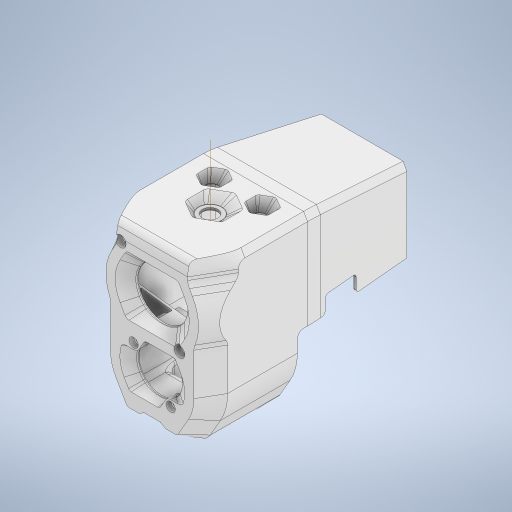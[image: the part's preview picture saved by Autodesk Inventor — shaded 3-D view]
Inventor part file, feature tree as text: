
AUTODESK INVENTOR PART (.ipt)
format: ipt  version: 2024 (Build 280153000, 153)  size: 3,584,000 bytes
history: native  units: mm
features: extrude x39, projected_geometry x35, plane x22, fillet x16, sketch x14, other x8, loft x5, hole x5, sweep x4, mirror x4, shell x4, boolean_combine x3, thicken_offset x3, chamfer x2, surface_op x2, split x1
ambient origin geometry x8: Origin, YZ Plane, XZ Plane, XY Plane, X Axis, Y Axis, Z Axis, Center Point
bodies: Solid1 (feature_tree), Solid4 (feature_tree), Solid5 (feature_tree), Solid2 (feature_tree), Solid3 (feature_tree)
feature tree (167):
  sketch  "Sketch1"  dims[d0=29.0mm d1=24.0mm]
  plane  "Work Plane10"
  extrude  "Extrusion1"  Depth=24.0mm
  plane  "Work Plane1"
  extrude  "Extrusion3"  Depth=7.25mm
  extrude  "Extrusion4"  Depth=33.0mm
  extrude  "Extrusion5"  Depth=30.0mm
  extrude  "Extrusion6"  Depth=20.0mm
  plane  "Work Plane12"
  extrude  "Extrusion16"  Depth=20.0mm
  plane  "Work Plane13"
  plane  "Work Plane14"
  sketch  "3D Sketch3"
  plane  "Work Plane3"
  extrude  "Extrusion17"  Depth=1.22173mm
  extrude  "Extrusion18"  Depth=0.25mm
  plane  "Work Plane15"
  sweep  "Sweep7"
  sketch  "3D Sketch5"
  sweep  "Sweep8"
  sweep  "Sweep9"
  mirror  "Mirror5"
  chamfer  "Chamfer4"  Distance=10.0mm
  sweep  "Sweep11"
  extrude  "Extrusion7"  Depth=35.0mm
  extrude  "Extrusion8"  Depth=3.0mm
  fillet  "Fillet3"  Radius=15.1mm
  other  "BOTTOM OF PRINTHEAD BASE"
  plane  "Work Plane6"
  extrude  "Extrusion19"  Depth=4.2mm
  plane  "Work Plane8"
  extrude  "Extrusion14"  TaperAngle=45.0deg  [1 undecoded]
  loft  "Loft1"
  plane  "Work Plane9"
  extrude  "Extrusion15"  TaperAngle=150.0deg  [1 undecoded]
  extrude  "Extrusion11"  TaperAngle=150.0deg  [1 undecoded]
  loft  "Loft2"
  extrude  "Extrusion13"  Depth=38.0mm
  other  "Work Axis1"
  plane  "Work Plane16"
  extrude  "Extrusion20"  Depth=110.0mm
  extrude  "Extrusion21"  Depth=6.0mm TaperAngle=0.0deg
  fillet  "Fillet4"  Radius=130.0mm
  fillet  "Fillet5"  Radius=48.0mm
  plane  "Work Plane17"
  extrude  "Extrusion23"  Depth=42.0mm
  plane  "Work Plane18"
  extrude  "Extrusion24"  Depth=2.0mm
  mirror  "Mirror6"
  extrude  "Extrusion25"  Depth=2.5mm
  mirror  "Mirror7"
  extrude  "Extrusion26"  Depth=2.0mm
  sketch  "Sketch49"  dims[d3=25.4mm d4=7.25mm]
  split  "Split1"
  shell  "Shell2"  Thickness=2.5mm
  extrude  "Extrusion36"  Depth=21.0mm
  shell  "Shell4"  Thickness=120.0deg
  extrude  "Extrusion27"  Depth=24.0mm
  extrude  "Extrusion28"  TaperAngle=120.0deg  [1 undecoded]
  extrude  "Extrusion30"  TaperAngle=120.0deg  [1 undecoded]
  extrude  "Extrusion29"  Depth=2.0mm
  extrude  "Extrusion31"  Depth=3.0mm
  extrude  "Extrusion32"  Depth=6.0mm
  extrude  "Extrusion33"  Depth=64.0mm
  extrude  "Extrusion34"  Depth=54.0mm
  boolean_combine  "Combine1"
  plane  "Work Plane20"
  fillet  "Fillet13"  Radius=2.0mm
  extrude  "Extrusion37"  Depth=8.0mm
  fillet  "Fillet12"  Radius=30.0mm
  plane  "Work Plane22"
  hole  "Hole3"  [1 undecoded]
  hole  "Hole4"  [1 undecoded]
  hole  "Hole5"  [1 undecoded]
  plane  "Work Plane23"
  hole  "Hole6"  [1 undecoded]
  fillet  "Fillet14"  Radius=8.0mm
  extrude  "Extrusion38"  Depth=35.0mm
  fillet  "Fillet15"  [1 undecoded]
  fillet  "Fillet16"  Radius=24.0mm
  extrude  "EXTRUDER ACCESS MIDPLANE"  Depth=2.0mm
  plane  "Work Plane25"
  plane  "Work Plane26"
  sketch  "Sketch83"  dims[d9=42.0mm d10=20.0mm]
  other  "Work Axis2"
  plane  "Work Plane31"
  plane  "Work Plane34"
  sketch  "Sketch84"  dims[d11=23.0mm d12=20.0mm]
  plane  "Work Plane32"
  sketch  "Sketch85"  dims[d13=18.0mm d14=1.22173mm]
  surface_op  "Stitch Surface2"
  extrude  "Extrusion48"  Depth=25.0mm
  fillet  "Fillet24"  Radius=70.0mm
  thicken_offset  "Thicken8"
  sketch  "Sketch86"  dims[d15=3.0mm d16=0.25mm]
  loft  "Loft3"
  shell  "Shell5"  Thickness=12.0mm
  extrude  "Extrusion51"  Depth=10.0mm TaperAngle=0.0deg
  boolean_combine  "Combine2"
  fillet  "Fillet26"  Radius=10.0mm
  hole  "Hole10"  [1 undecoded]
  fillet  "Fillet27"  [1 undecoded]
  sketch  "Sketch90"  dims[d23=1.5mm d24=0.25mm]
  loft  "Loft4"
  shell  "Shell6"  Thickness=4.0mm
  extrude  "Extrusion53"  Depth=12.0mm
  boolean_combine  "Combine3"
  extrude  "Extrusion52"  TaperAngle=0.0deg  [1 undecoded]
  fillet  "Fillet28"  Radius=6.0mm
  chamfer  "Chamfer5"  Angle=90.0deg  [1 undecoded]
  thicken_offset  "Thicken7"
  fillet  "Fillet21"  [1 undecoded]
  fillet  "Fillet22"  Radius=1.0mm
  thicken_offset  "Thicken3"
  sketch  "Sketch73"  dims[d7=30.0mm d8=30.0mm]
  extrude  "Extrusion39"  Depth=1.0mm
  mirror  "Mirror10"
  extrude  "Extrusion40"  Depth=5.0mm TaperAngle=0.0deg
  fillet  "Fillet7"  [1 undecoded]
  fillet  "Fillet8"  [1 undecoded]
  projected_geometry  "Projected Loop3"
  projected_geometry  "Projected Loop6"
  projected_geometry  "Projected Loop7"
  other  "Edges2"
  projected_geometry  "Projected Loop10"
  other  "Edges3"
  projected_geometry  "Projected Loop11"
  plane  "Work Plane11"
  projected_geometry  "Projected Loop12"
  projected_geometry  "Projected Loop15"
  projected_geometry  "Projected Loop16"
  projected_geometry  "Projected Loop17"
  projected_geometry  "Projected Loop18"
  projected_geometry  "Projected Loop19"
  projected_geometry  "Projected Loop20"
  projected_geometry  "Projected Loop21"
  projected_geometry  "Projected Loop25"
  projected_geometry  "Projected Loop26"
  projected_geometry  "Projected Loop27"
  projected_geometry  "Projected Loop28"
  projected_geometry  "Projected Loop29"
  projected_geometry  "Projected Loop30"
  projected_geometry  "Projected Loop31"
  projected_geometry  "Projected Loop32"
  sketch  "Sketch60"  dims[d5=27.75mm d6=33.0mm]
  projected_geometry  "Projected Loop34"
  projected_geometry  "Projected Loop35"
  other  "Srf7"
  other  "Srf8"
  other  "Srf9"
  sketch  "Sketch87"  dims[d18=3.25mm d20=2.0mm]
  sketch  "Sketch89"  dims[d21=1.5mm d22=0.25mm]
  projected_geometry  "Projected Loop39"
  sketch  "Sketch91"  dims[d25=35.0mm d26=10.0mm d27=35.0mm d28=35.0mm d29=3.0mm d30=15.1mm d32=4.2mm d33=45.0deg d34=1.0mm d35=150.0deg d36=150.0deg d37=4.0mm d38=38.0mm d40=110.0mm d42=6.0mm d43=0.0mm d44=130.0mm d45=0.0mm d62=48.0mm d63=42.0mm d64=2.0mm d65=2.5mm d66=2.0mm d67=2.5mm d72=21.0mm d73=120.0deg d74=24.0mm d75=120.0deg d76=120.0deg d77=2.0mm d78=3.0mm d80=6.0mm d81=64.0mm d83=54.0mm d84=2.0mm d85=8.0mm d86=30.0mm d87=8.0mm d88=8.0mm d89=6.0mm d90=0.0mm d95=-12.0mm d99=8.0mm d100=35.0mm d101=30.0deg d102=24.0mm d103=2.0mm d104=25.0mm d106=70.0mm d107=110.0mm d109=12.0mm d110=0.0mm d111=10.0mm d112=0.0mm d113=10.0mm d114=0.0mm d115=8.0mm d127=0.0mm d128=0.0mm d130=0.0mm d131=0.0mm d133=4.0mm d136=12.0mm d137=-53.0mm d144=0.0mm d145=90.0deg d147=6.0mm d148=0.0mm d149=0.0mm d150=90.0deg d151=0.0mm d152=90.0deg d155=1.0mm d156=0.0mm d157=1.0mm d158=5.0mm d159=0.0mm d160=0.0mm d161=90.0deg d162=-1.5mm d163=6.0mm d164=0.0mm d165=15.0mm d166=46.5mm d167=-31.5mm d168=4.0mm d169=10.0mm d170=60.0deg d171=10.0mm d172=6.0mm d173=16.306mm d174=0.0mm d183=50.0mm d184=75.0mm d185=0.0mm d186=0.0mm d187=0.0mm d188=0.0mm d189=30.0mm d190=30.0deg d191=0.0mm d192=0.0mm d193=0.0mm d194=0.0mm d195=0.0mm d196=0.0mm d199=0.0mm d200=0.0mm d202=59.03mm d203=0.0mm d204=-17.0mm d205=30.5mm d206=30.5mm d207=3.0mm d208=10.0mm d209=0.0mm d210=28.0mm d211=10.0mm d212=0.0mm d213=4.0mm d214=4.0mm d220=17.7mm d221=13.0mm d222=11.0mm d223=0.0mm d224=10.0mm d225=0.0mm d227=-13.0mm d228=1.5mm d229=10.0mm d230=0.0mm d231=1.5mm d232=1.5mm d233=1.5mm d234=16.0mm d235=10.0mm d236=0.0mm d237=32.0mm d238=8.0mm d239=0.0mm d240=1.5mm d242=1.5mm d244=1.5mm d245=2.0mm d246=2.0mm d247=1.5mm d248=10.0mm d249=0.0mm d250=6.323mm d251=0.0mm d252=10.0mm d253=0.0mm d254=0.0mm d256=1.5mm d257=0.0mm d259=1.5mm d260=0.0mm d261=1.5mm d262=0.0mm d263=17.0mm d264=8.0mm d265=2.01mm d266=0.0mm d267=0.0mm d268=0.800116mm d269=0.5mm d270=8.0mm d271=0.0mm d280=8.0mm d281=0.0mm d283=1.5mm d284=19.451625mm d290=10.0mm d291=0.0mm d293=-1.5mm d294=24.0mm d295=24.0mm d296=8.0mm d297=60.0deg d300=2.0mm d315=1.0mm d316=60.0deg d317=60.0deg d318=60.0deg d319=24.0mm d320=24.0mm d321=-2.0mm d322=6.0mm d323=6.0mm d324=6.5mm d325=3.0mm d326=14.3117mm d327=3.0mm d328=0.0mm d329=3.2mm d330=6.0mm d331=6.5mm d332=3.0mm d333=14.3117mm d334=8.0mm d335=0.0mm d336=4.3mm d337=6.0mm d338=8.0mm d339=4.0mm d340=14.3117mm d341=8.0mm d342=0.0mm d343=-4.0mm d344=7.0mm d345=6.0mm d346=8.0mm d347=4.0mm d348=14.3117mm d349=8.0mm d350=0.0mm d351=1.0mm d352=11.0mm d353=22.0mm d354=33.645mm d355=0.0mm d356=82.75mm d357=2.0mm d358=4.0mm d359=-27.5mm d360=8.15mm d361=-8.15mm d388=0.5mm d389=0.5mm d390=10.0mm d391=0.0mm d392=10.0mm d393=0.0mm d438=1.0mm d439=1.0mm d459=15.6mm d460=16.32mm d461=59.5mm d462=15.0mm d463=8.0mm d464=4.5mm d466=2.0mm d467=24.0mm d468=2.5mm d469=2.0mm d470=3.0mm d471=120.0deg d472=2.0mm d473=0.0mm d474=90.0deg d475=0.0mm d476=90.0deg d477=5.0mm d478=0.0mm d479=10.0mm d480=0.0mm d481=1.5mm d482=1.5mm d483=0.5mm d484=1.5mm d485=1.5mm d506=10.0mm d507=6.0mm d508=4.0mm d509=2.0mm d510=90.0deg d511=8.0mm d512=0.0mm d513=1.5mm d514=2.0mm d515=45.0deg d519=0.0mm d520=90.0deg d521=0.0mm d522=90.0deg d523=0.5mm d532=1.5mm d533=10.0mm d534=0.0mm d535=-2.5mm d536=0.25mm d537=2.0mm d538=10.0mm d539=0.0mm d540=0.0mm d541=90.0deg d542=0.0mm d543=90.0deg d544=1.5mm d545=10.0mm d546=0.0mm d547=0.5mm d499=1.0mm d500=1.0mm d501=1.0mm d502=0.15mm d503=0.25mm d504=0.375mm d505=14.3117mm]
  projected_geometry  "Project Cut Edges1"
  projected_geometry  "Project Cut Edges2"
  projected_geometry  "Project Cut Edges4"
  projected_geometry  "Project Cut Edges5"
  projected_geometry  "Project Cut Edges6"
  projected_geometry  "Project Cut Edges7"
  projected_geometry  "Project Cut Edges8"
  projected_geometry  "Project Cut Edges9"
  projected_geometry  "Project Cut Edges10"
  projected_geometry  "Project Cut Edges11"
  projected_geometry  "Project Cut Edges13"
  loft  "LoftSrf1"
  surface_op  "Boundary Patch1"
note: 17 required parameter values undecoded (feature->parameter linkage not recoverable at this tier; creation-order binding heuristic only, values carry confidence <= 0.55)
